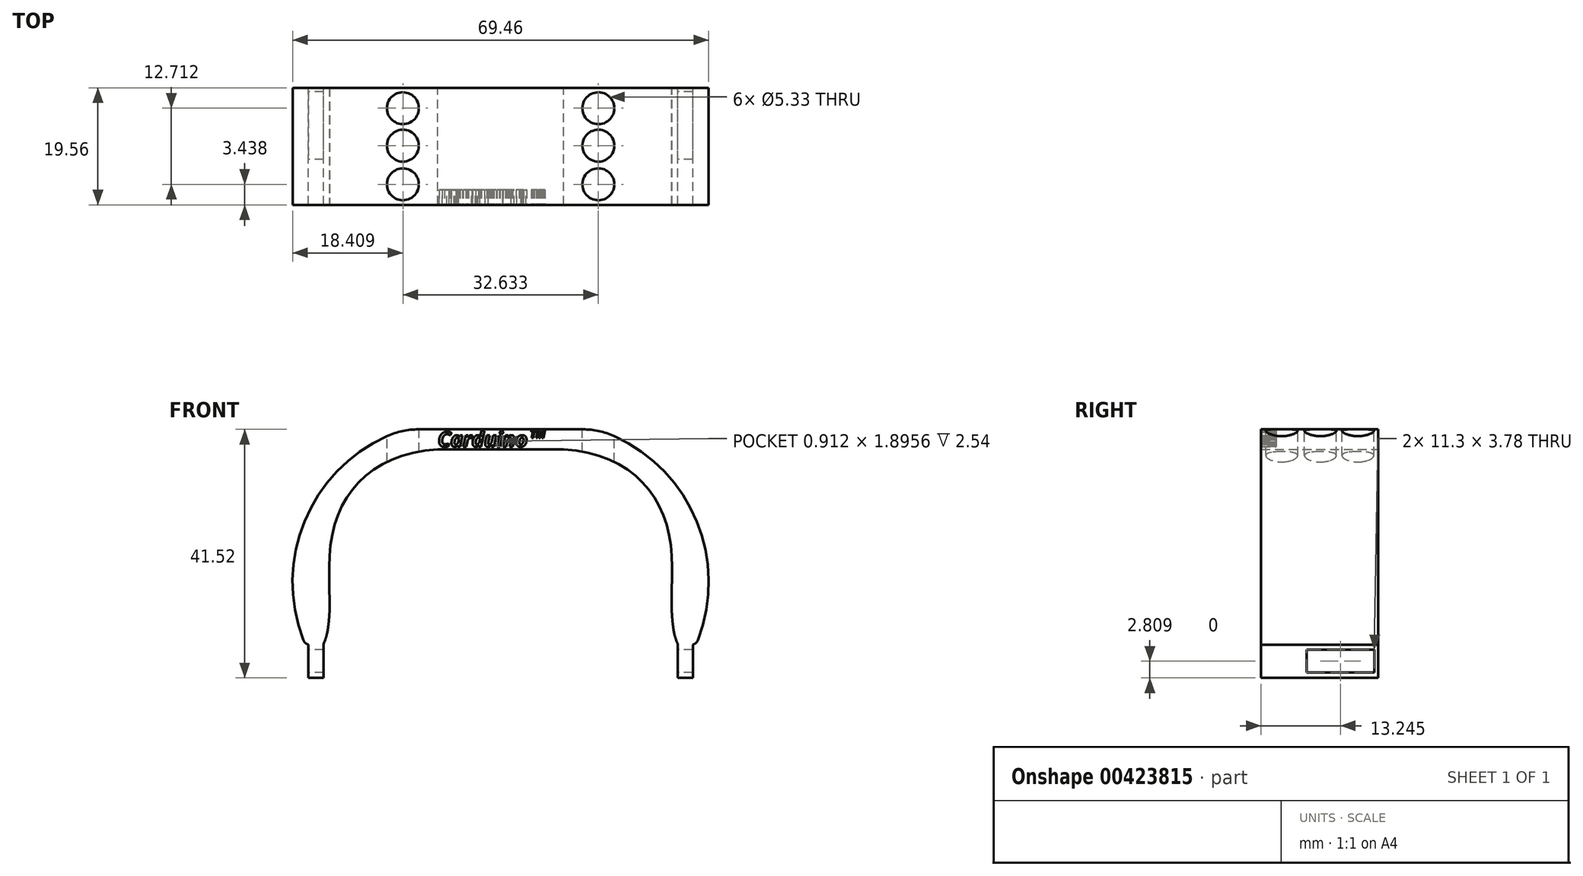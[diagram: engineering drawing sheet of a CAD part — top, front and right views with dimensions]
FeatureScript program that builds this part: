
annotation { "Feature Type Name" : "Feature", "Feature Type Description" : "" }
export const myFeature = defineFeature(function(context is Context, id is Id, definition is map)
    precondition{}
    {
        {
            var Q0;
            Q0=qCreatedBy(makeId("Front.planeOp"),FACE);
            var sketch = newSketch(context, id + "F0", { "sketchPlane" : qUnion([Q0])});
            skPoint(sketch, "E0", {"position": v(7.6, 18.16) * mm});
            skPoint(sketch, "E1.end.orphan", {"position": v(28.65, 16.3) * mm});
            skLineSegment(sketch, "E2.MirrorCS", {"start": v(7.96, 19.63) * mm, "end": v(8.8, 19.63) * mm});
            skLineSegment(sketch, "E3.MirrorCS", {"start": v(8.8, 19.63) * mm, "end": v(21.34, 19.63) * mm});
            skArc(sketch, "E4.MirrorCS", {"start": v(26.57, 18.5) * mm, "mid": v(40.33, 4.25) * mm, "end": v(40.54, -15.57) * mm});
            skFitSpline(sketch, "E5.MirrorCS", {"points": [v(15.98, 16.37) * mm, v(36.04, -0.09) * mm, v(43.29, -19.57) * mm], "startDerivative": vector(70.47, 0) * mm, "endDerivative": vector(62.33, 0) * mm});
            skArc(sketch, "E6.filletArc", {"start": v(36.47, -13.91) * mm, "mid": v(36.7, -14.44) * mm, "end": v(37.15, -14.81) * mm});
            skPoint(sketch, "E7.visualSharp", {"position": v(40.56, -15.51) * mm});
            skArc(sketch, "E7.filletArc", {"start": v(39.79, -16.3) * mm, "mid": v(40.25, -16.01) * mm, "end": v(40.54, -15.57) * mm});
            skPoint(sketch, "E8.orphan", {"position": v(39.69, -14.3) * mm});
            skPoint(sketch, "E9.MirrorCS.start.orphan", {"position": v(39.79, -16.3) * mm});
            skLineSegment(sketch, "E10.MirrorCS", {"start": v(37.15, -15.02) * mm, "end": v(37.15, -21.9) * mm});
            skLineSegment(sketch, "E11.MirrorCS", {"start": v(39.69, -16.33) * mm, "end": v(39.69, -21.9) * mm});
            skLineSegment(sketch, "E12.MirrorCS", {"start": v(39.69, -21.9) * mm, "end": v(37.15, -21.9) * mm});
            skLineSegment(sketch, "E13", {"start": v(7.6, 16.3) * mm, "end": v(18.13, 16.3) * mm});
            skPoint(sketch, "E14.visualSharp", {"position": v(23.62, 19.63) * mm});
            skArc(sketch, "E14.filletArc", {"start": v(26.57, 18.5) * mm, "mid": v(24.01, 19.35) * mm, "end": v(21.34, 19.63) * mm});
            skLineSegment(sketch, "E15", {"start": v(7.6, 16.3) * mm, "end": v(7.6, 19.63) * mm});
            skLineSegment(sketch, "E16", {"start": v(7.6, 19.63) * mm, "end": v(7.96, 19.63) * mm});
            skFitSpline(sketch, "E17.MirrorCS", {"points": [v(-0.77, 16.37) * mm, v(-20.83, -0.09) * mm, v(-28.08, -19.57) * mm], "startDerivative": vector(-70.47, 0) * mm, "endDerivative": vector(-62.33, 0) * mm});
            skLineSegment(sketch, "E18.MirrorCS", {"start": v(7.6, 16.3) * mm, "end": v(-2.92, 16.3) * mm});
            skLineSegment(sketch, "E19.MirrorCS", {"start": v(6.42, 19.63) * mm, "end": v(-6.13, 19.63) * mm});
            skArc(sketch, "E20.MirrorCS", {"start": v(-11.36, 18.5) * mm, "mid": v(-25.12, 4.25) * mm, "end": v(-25.33, -15.57) * mm});
            skArc(sketch, "E21.MirrorCS", {"start": v(-11.36, 18.5) * mm, "mid": v(-8.8, 19.35) * mm, "end": v(-6.13, 19.63) * mm});
            skLineSegment(sketch, "E22.MirrorCS", {"start": v(-21.94, -15.02) * mm, "end": v(-21.94, -21.9) * mm});
            skLineSegment(sketch, "E23.MirrorCS", {"start": v(7.6, 19.63) * mm, "end": v(7.25, 19.63) * mm});
            skLineSegment(sketch, "E24.MirrorCS", {"start": v(-24.48, -16.33) * mm, "end": v(-24.48, -21.9) * mm});
            skLineSegment(sketch, "E25.MirrorCS", {"start": v(7.25, 19.63) * mm, "end": v(6.42, 19.63) * mm});
            skLineSegment(sketch, "E26.MirrorCS", {"start": v(-24.48, -21.9) * mm, "end": v(-21.94, -21.9) * mm});
            skArc(sketch, "E27.MirrorCS", {"start": v(-21.25, -13.91) * mm, "mid": v(-21.49, -14.44) * mm, "end": v(-21.94, -14.81) * mm});
            skArc(sketch, "E28.MirrorCS", {"start": v(-24.58, -16.3) * mm, "mid": v(-25.04, -16.01) * mm, "end": v(-25.33, -15.57) * mm});
            skLineSegment(sketch, "E29", {"start": v(-24.58, -16.3) * mm, "end": v(-24.48, -16.33) * mm});
            skLineSegment(sketch, "E30", {"start": v(-21.94, -14.81) * mm, "end": v(-21.94, -15.02) * mm});
            skPoint(sketch, "E31.orphan", {"position": v(-24.48, -15.54) * mm});
            skLineSegment(sketch, "E32", {"start": v(37.15, -14.81) * mm, "end": v(37.15, -15.02) * mm});
            skLineSegment(sketch, "E33", {"start": v(39.79, -16.3) * mm, "end": v(39.69, -16.33) * mm});
            skPoint(sketch, "E34.orphan", {"position": v(39.69, -15.54) * mm});
            skSolve(sketch);
        }
        {
            var Q0;
            Q0 = qSketchRegion(id + "F0", true);
            extrude(context, id + "F1", {"entities" : qUnion([Q0]), "depth" : 19.56 * mm});
        }
        {
            var Q0;
            Q0=makeQuery(id+"F1.opExtrude","CAP_FACE",FACE,{"disambiguationData":[OSD([sQuery(id+"F0.wireOp",EDGE,"E2.MirrorCS"),sQuery(id+"F0.wireOp",EDGE,"E3.MirrorCS"),sQuery(id+"F0.wireOp",EDGE,"E4.MirrorCS"),sQuery(id+"F0.wireOp",EDGE,"E5.MirrorCS"),sQuery(id+"F0.wireOp",EDGE,"E6.filletArc"),sQuery(id+"F0.wireOp",EDGE,"E7.filletArc"),sQuery(id+"F0.wireOp",EDGE,"E10.MirrorCS"),sQuery(id+"F0.wireOp",EDGE,"E11.MirrorCS"),sQuery(id+"F0.wireOp",EDGE,"E12.MirrorCS"),sQuery(id+"F0.wireOp",EDGE,"E13"),sQuery(id+"F0.wireOp",EDGE,"E14.filletArc"),sQuery(id+"F0.wireOp",EDGE,"E16"),sQuery(id+"F0.wireOp",EDGE,"E18.MirrorCS"),sQuery(id+"F0.wireOp",EDGE,"E19.MirrorCS"),sQuery(id+"F0.wireOp",EDGE,"E17.MirrorCS"),sQuery(id+"F0.wireOp",EDGE,"E20.MirrorCS"),sQuery(id+"F0.wireOp",EDGE,"E21.MirrorCS"),sQuery(id+"F0.wireOp",EDGE,"E22.MirrorCS"),sQuery(id+"F0.wireOp",EDGE,"E23.MirrorCS"),sQuery(id+"F0.wireOp",EDGE,"E24.MirrorCS"),sQuery(id+"F0.wireOp",EDGE,"E25.MirrorCS"),sQuery(id+"F0.wireOp",EDGE,"E26.MirrorCS"),sQuery(id+"F0.wireOp",EDGE,"E27.MirrorCS"),sQuery(id+"F0.wireOp",EDGE,"E28.MirrorCS"),sQuery(id+"F0.wireOp",EDGE,"E29"),sQuery(id+"F0.wireOp",EDGE,"E30"),sQuery(id+"F0.wireOp",EDGE,"E32"),sQuery(id+"F0.wireOp",EDGE,"E33")])],"isStart":false});
            var sketch = newSketch(context, id + "F2", { "sketchPlane" : qUnion([Q0])});
            skText(sketch, "E35", { "text": "Carduino\n", "fontName": "OpenSans-BoldItalic.ttf"});
            skText(sketch, "E36", { "text": "TM", "fontName": "OpenSans-BoldItalic.ttf"});
            const initialGuessF2  = {"E35": [-0.00288, 0.01673, 1, 0, 0.0025], "E36": [0.01256, 0.0182, 1, 0, 0.00125]};
            skSetInitialGuess(sketch, initialGuessF2);
            skSolve(sketch);
        }
        {
            var Q0;
            Q0=makeQuery(id+"F1.opExtrude","SWEPT_FACE",FACE,{"disambiguationData":[OSD([sQuery(id+"F0.wireOp",EDGE,"E24.MirrorCS")])]});
            var sketch = newSketch(context, id + "F3", { "sketchPlane" : qUnion([Q0])});
            skLineSegment(sketch, "E37.bottom", {"start": v(0.66, -17.19) * mm, "end": v(11.97, -17.19) * mm});
            skLineSegment(sketch, "E37.top", {"start": v(0.66, -20.97) * mm, "end": v(11.97, -20.97) * mm});
            skLineSegment(sketch, "E37.left", {"start": v(0.66, -17.19) * mm, "end": v(0.66, -20.97) * mm});
            skLineSegment(sketch, "E37.right", {"start": v(11.97, -17.19) * mm, "end": v(11.97, -20.97) * mm});
            skSolve(sketch);
        }
        {
            var Q0;
            Q0 = qSketchRegion(id + "F3", true);
            extrude(context, id + "F4", {"entities" : qUnion([Q0]), "operationType" : NewBodyOperationType.REMOVE, "oppositeDirection" : true, "depth" : 127 * mm});
        }
        {
            var Q0;
            Q0 = qSketchRegion(id + "F2", true);
            extrude(context, id + "F5", {"entities" : qUnion([Q0]), "operationType" : NewBodyOperationType.REMOVE, "oppositeDirection" : true, "depth" : 2.54 * mm});
        }
        {
            var Q0;
            Q0=makeQuery(id+"F1.opExtrude","SWEPT_FACE",FACE,{"disambiguationData":[OSD([sQuery(id+"F0.wireOp",EDGE,"E2.MirrorCS"),sQuery(id+"F0.wireOp",EDGE,"E3.MirrorCS"),sQuery(id+"F0.wireOp",EDGE,"E16"),sQuery(id+"F0.wireOp",EDGE,"E19.MirrorCS"),sQuery(id+"F0.wireOp",EDGE,"E23.MirrorCS"),sQuery(id+"F0.wireOp",EDGE,"E25.MirrorCS")])]});
            var sketch = newSketch(context, id + "F6", { "sketchPlane" : qUnion([Q0])});
            skCircle(sketch, "E38", {"center": v(-8.71, -3.41) * mm, "radius": 2.67 * mm});
            skCircle(sketch, "E39", {"center": v(-8.71, -9.67) * mm, "radius": 2.67 * mm});
            skCircle(sketch, "E40", {"center": v(-8.71, -16.12) * mm, "radius": 2.67 * mm});
            skPoint(sketch, "E41", {"position": v(7.6, 0) * mm});
            skLineSegment(sketch, "E42", {"start": v(7.6, 0) * mm, "end": v(7.6, -19.56) * mm});
            skCircle(sketch, "E43.MirrorC", {"center": v(23.92, -3.41) * mm, "radius": 2.67 * mm});
            skCircle(sketch, "E44.MirrorC", {"center": v(23.92, -9.67) * mm, "radius": 2.67 * mm});
            skCircle(sketch, "E45.MirrorC", {"center": v(23.92, -16.12) * mm, "radius": 2.67 * mm});
            skSolve(sketch);
        }
        {
            var Q0;
            Q0 = qSketchRegion(id + "F6", true);
            extrude(context, id + "F7", {"entities" : qUnion([Q0]), "operationType" : NewBodyOperationType.REMOVE, "oppositeDirection" : true, "depth" : 25.4 * mm});
        }
    });
